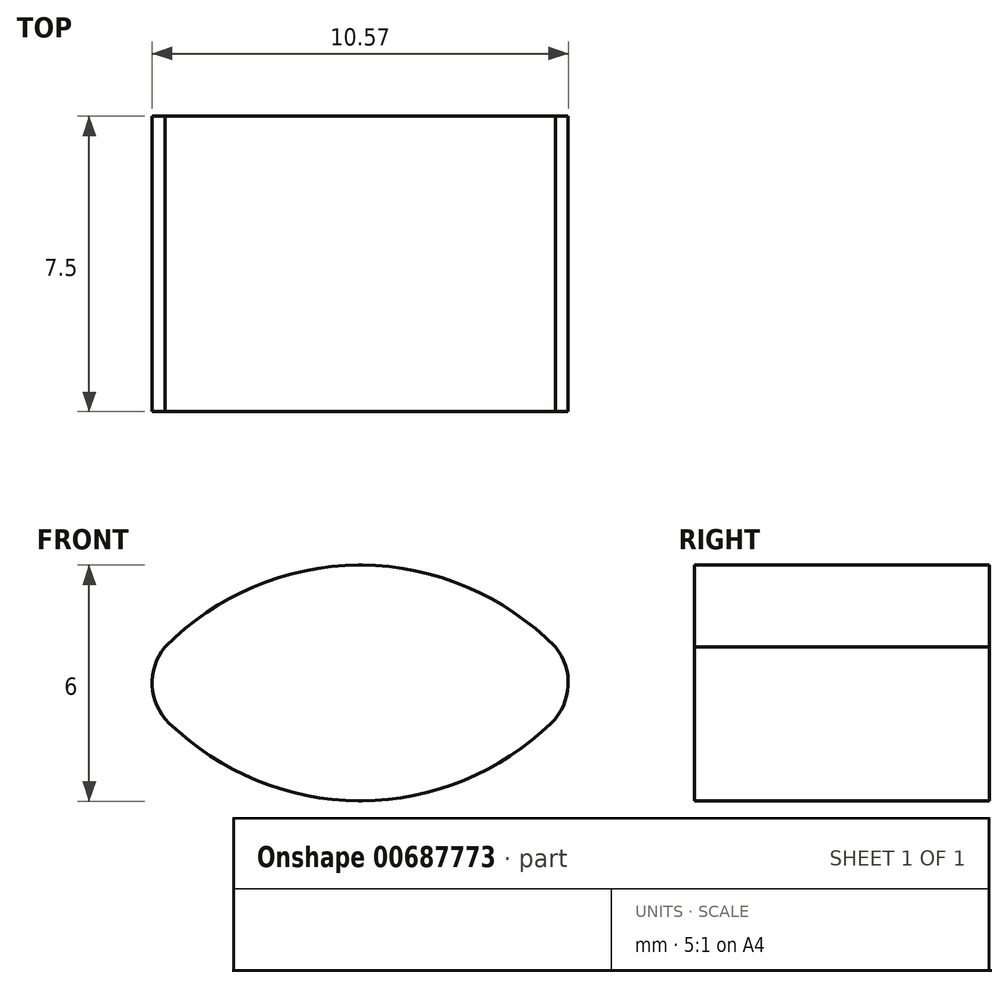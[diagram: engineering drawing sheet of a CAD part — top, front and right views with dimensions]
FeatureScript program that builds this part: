
annotation { "Feature Type Name" : "Feature", "Feature Type Description" : "" }
export const myFeature = defineFeature(function(context is Context, id is Id, definition is map)
    precondition{}
    {
        {
            var Q0;
            Q0=qCreatedBy(makeId("Front.planeOp"),FACE);
            var sketch = newSketch(context, id + "F0", { "sketchPlane" : qUnion([Q0])});
            skCircle(sketch, "E0", {"center": v(0.16, -0.3) * mm, "radius": 3 * mm});
            skPoint(sketch, "E0.centerSnap0", {"position": v(0.16, 3.44) * mm});
            skPoint(sketch, "E0.centerSnap1", {"position": v(-7.34, -0.3) * mm});
            skArc(sketch, "E1", {"start": v(5.12, 0.6) * mm, "mid": v(2.85, 2.15) * mm, "end": v(0.16, 2.7) * mm});
            skArc(sketch, "E2", {"start": v(0.16, -3.3) * mm, "mid": v(2.78, -2.79) * mm, "end": v(5.01, -1.33) * mm});
            skArc(sketch, "E3", {"start": v(5.01, -1.33) * mm, "mid": v(5.45, -0.38) * mm, "end": v(5.12, 0.6) * mm});
            skPoint(sketch, "E4.orphan", {"position": v(5.88, -0.3) * mm});
            skLineSegment(sketch, "E5", {"start": v(0.16, 2.85) * mm, "end": v(0.16, -3.79) * mm, "construction": true});
            skArc(sketch, "E6.MirrorCS", {"start": v(-4.8, 0.6) * mm, "mid": v(-2.52, 2.15) * mm, "end": v(0.16, 2.7) * mm});
            skArc(sketch, "E7.MirrorCS", {"start": v(-4.69, -1.33) * mm, "mid": v(-5.12, -0.38) * mm, "end": v(-4.8, 0.6) * mm});
            skArc(sketch, "E8.MirrorCS", {"start": v(0.16, -3.3) * mm, "mid": v(-2.45, -2.79) * mm, "end": v(-4.69, -1.33) * mm});
            skSolve(sketch);
        }
        {
            var Q0;
            Q0 = qSketchRegion(id + "F0", true);
            extrude(context, id + "F1", {"entities" : qUnion([Q0]), "depth" : 7.5 * mm, "offsetDistance" : 25 * mm});
        }
    });
